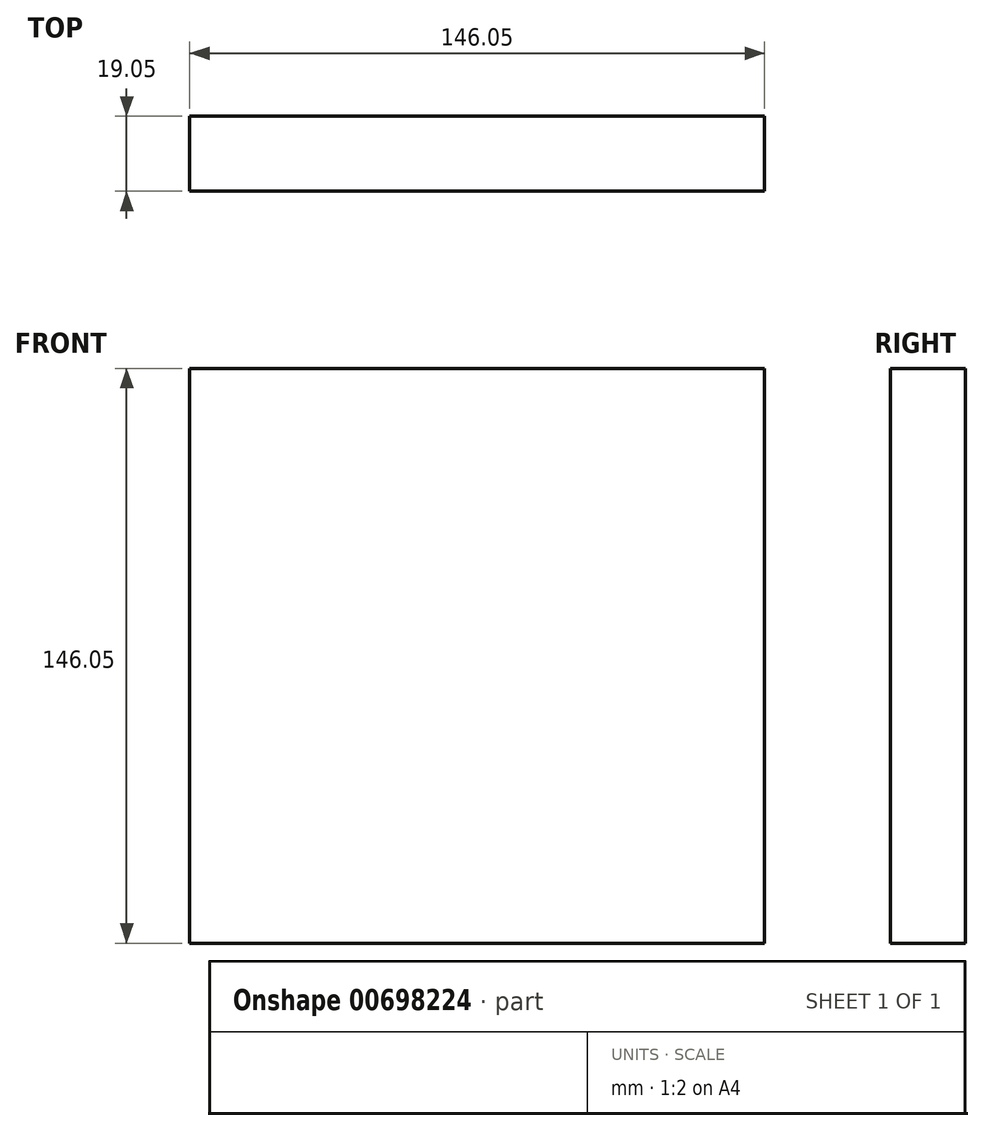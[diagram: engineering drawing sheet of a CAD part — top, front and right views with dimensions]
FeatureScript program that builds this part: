
annotation { "Feature Type Name" : "Feature", "Feature Type Description" : "" }
export const myFeature = defineFeature(function(context is Context, id is Id, definition is map)
    precondition{}
    {
        {
            var Q0;
            Q0=qCreatedBy(makeId("Front.planeOp"),FACE);
            var sketch = newSketch(context, id + "F0", { "sketchPlane" : qUnion([Q0])});
            skLineSegment(sketch, "E0.bottom", {"start": v(-181.9, -89.75) * mm, "end": v(-35.85, -89.75) * mm});
            skLineSegment(sketch, "E0.top", {"start": v(-181.9, -235.8) * mm, "end": v(-35.85, -235.8) * mm});
            skLineSegment(sketch, "E0.left", {"start": v(-181.9, -89.75) * mm, "end": v(-181.9, -235.8) * mm});
            skLineSegment(sketch, "E0.right", {"start": v(-35.85, -89.75) * mm, "end": v(-35.85, -235.8) * mm});
            skSolve(sketch);
        }
        {
            var Q0;
            Q0 = qSketchRegion(id + "F0", true);
            extrude(context, id + "F1", {"entities" : qUnion([Q0]), "depth" : 19.05 * mm, "offsetDistance" : 25.4 * mm});
        }
    });
